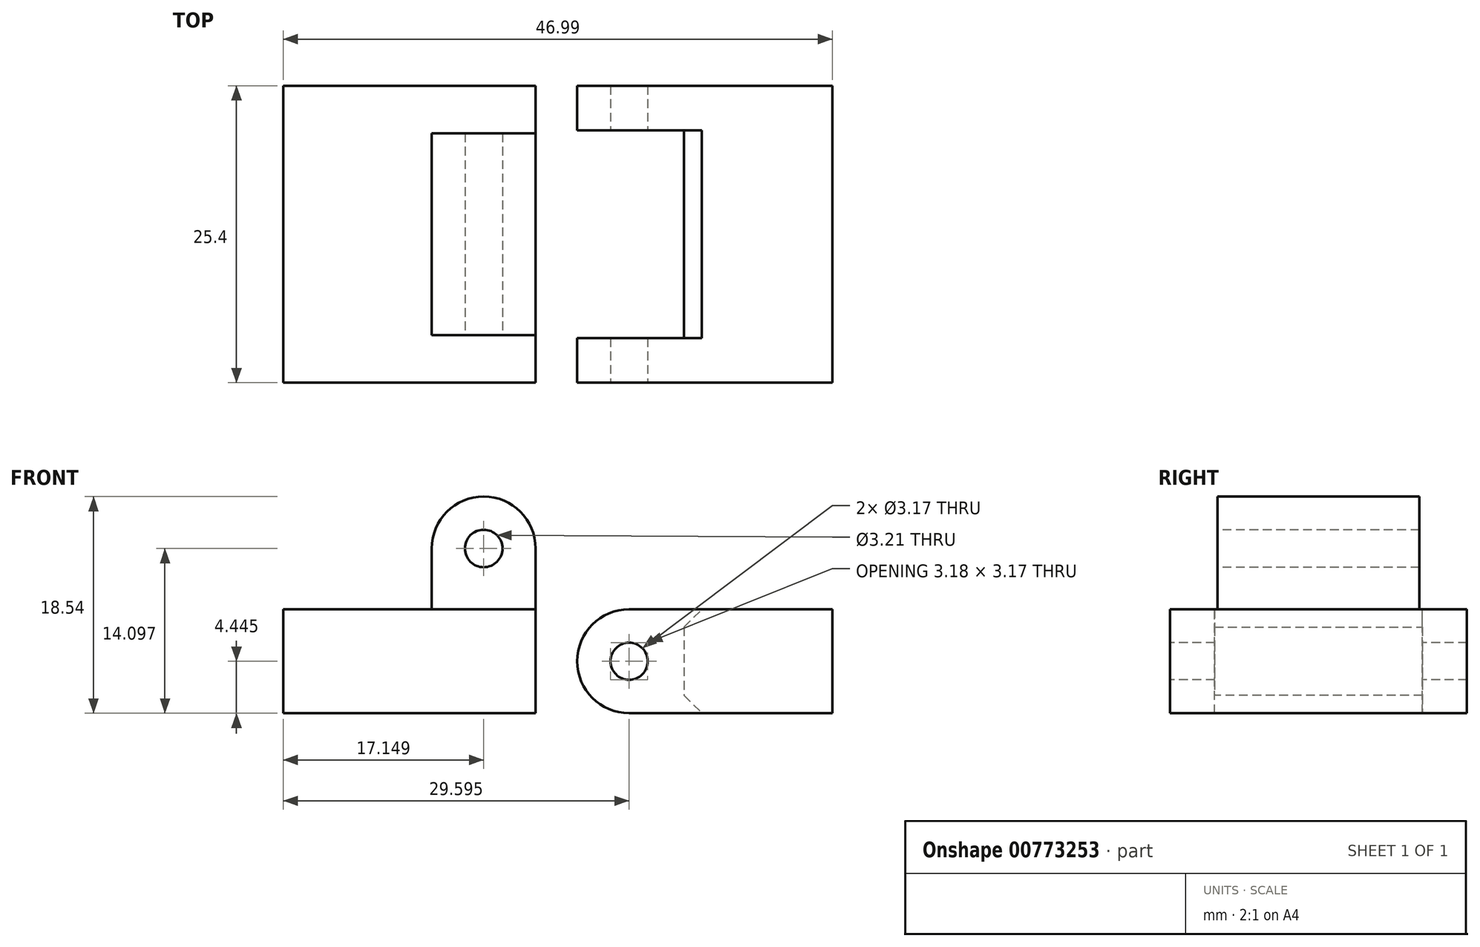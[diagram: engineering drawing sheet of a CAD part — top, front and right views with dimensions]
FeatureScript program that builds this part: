
annotation { "Feature Type Name" : "Feature", "Feature Type Description" : "" }
export const myFeature = defineFeature(function(context is Context, id is Id, definition is map)
    precondition{}
    {
        {
            var Q0;
            Q0=qCreatedBy(makeId("Top.planeOp"),FACE);
            var sketch = newSketch(context, id + "F0", { "sketchPlane" : qUnion([Q0])});
            skLineSegment(sketch, "E0.bottom", {"start": v(-16.8, 16.17) * mm, "end": v(-4.1, 16.17) * mm});
            skLineSegment(sketch, "E0.top", {"start": v(-16.8, -9.23) * mm, "end": v(-4.1, -9.23) * mm});
            skLineSegment(sketch, "E0.left", {"start": v(-16.8, 16.17) * mm, "end": v(-16.8, -9.23) * mm});
            skLineSegment(sketch, "E0.right", {"start": v(-4.1, 16.17) * mm, "end": v(-4.1, -9.23) * mm});
            skLineSegment(sketch, "E1", {"start": v(-16.8, 16.17) * mm, "end": v(-25.95, 16.17) * mm});
            skLineSegment(sketch, "E2", {"start": v(-16.8, -9.23) * mm, "end": v(-25.95, -9.23) * mm});
            skLineSegment(sketch, "E3", {"start": v(-25.95, -9.23) * mm, "end": v(-25.95, -5.42) * mm});
            skLineSegment(sketch, "E4", {"start": v(-25.95, -5.42) * mm, "end": v(-16.8, -5.42) * mm});
            skLineSegment(sketch, "E5", {"start": v(-25.95, 16.17) * mm, "end": v(-25.95, 12.36) * mm});
            skLineSegment(sketch, "E6", {"start": v(-25.95, 12.36) * mm, "end": v(-16.8, 12.36) * mm});
            skSolve(sketch);
        }
        {
            var Q0;
            {var subQ3=sQuery(id+"F0.wireOp",EDGE,"E0.bottom");Q0=makeQuery(id+"F0.imprint","IMPRINT",FACE,{"disambiguationData":[TD([[makeQuery(id+"F0.imprint","IMPRINT",EDGE,{"derivedFrom":subQ3}),-1.0]])]});}
            var Q1;
            {var subQ0=sQuery(id+"F0.wireOp",EDGE,"E1");Q1=makeQuery(id+"F0.imprint","IMPRINT",FACE,{"disambiguationData":[TD([[makeQuery(id+"F0.imprint","IMPRINT",EDGE,{"derivedFrom":subQ0}),1.0]])]});}
            var Q2;
            {var subQ0=sQuery(id+"F0.wireOp",EDGE,"E2");Q2=makeQuery(id+"F0.imprint","IMPRINT",FACE,{"disambiguationData":[TD([[makeQuery(id+"F0.imprint","IMPRINT",EDGE,{"derivedFrom":subQ0}),-1.0]])]});}
            extrude(context, id + "F1", {"entities" : qUnion([Q0, Q1, Q2]), "depth" : 8.9 * mm, "offsetDistance" : 25.4 * mm});
        }
        {
            var Q0;
            Q0=qCreatedBy(makeId("Top.planeOp"),FACE);
            var sketch = newSketch(context, id + "F2", { "sketchPlane" : qUnion([Q0])});
            skPoint(sketch, "E7.0", {"position": v(-25.95, 16.17) * mm});
            skPoint(sketch, "E7.1", {"position": v(-25.95, -9.23) * mm});
            skLineSegment(sketch, "E8", {"start": v(-38.4, 16.17) * mm, "end": v(-38.4, 12.1) * mm});
            skLineSegment(sketch, "E9", {"start": v(-38.4, 12.1) * mm, "end": v(-29.5, 12.1) * mm});
            skLineSegment(sketch, "E10", {"start": v(-38.4, 12.1) * mm, "end": v(-38.4, -9.23) * mm, "construction": true});
            skLineSegment(sketch, "E11", {"start": v(-38.4, -9.23) * mm, "end": v(-38.4, -5.17) * mm});
            skLineSegment(sketch, "E12", {"start": v(-38.4, -5.17) * mm, "end": v(-29.5, -5.17) * mm});
            skLineSegment(sketch, "E13", {"start": v(-29.5, -5.17) * mm, "end": v(-29.5, 12.1) * mm});
            skLineSegment(sketch, "E14", {"start": v(-38.4, 16.17) * mm, "end": v(-51.1, 16.17) * mm});
            skLineSegment(sketch, "E15", {"start": v(-51.1, 16.17) * mm, "end": v(-51.1, -9.23) * mm});
            skLineSegment(sketch, "E16", {"start": v(-51.1, -9.23) * mm, "end": v(-38.4, -9.23) * mm});
            skPoint(sketch, "E17.0", {"position": v(-16.8, 3.47) * mm});
            skLineSegment(sketch, "E18", {"start": v(-16.8, 3.47) * mm, "end": v(-29.5, 3.47) * mm, "construction": true});
            skSolve(sketch);
        }
        {
            var Q0;
            Q0=makeQuery(id+"F2.imprint","IMPRINT",FACE,{"disambiguationData":[TD([[makeQuery(id+"F2.imprint","IMPRINT",EDGE,{"derivedFrom":sQuery(id+"F2.wireOp",EDGE,"E8")}),-1.0]])]});
            extrude(context, id + "F3", {"entities" : qUnion([Q0]), "depth" : 8.9 * mm, "offsetDistance" : 25.4 * mm});
        }
        {
            var Q0;
            Q0=makeQuery(id+"F3.opExtrude","CAP_FACE",FACE,{"disambiguationData":[OSD([sQuery(id+"F2.wireOp",EDGE,"E8"),sQuery(id+"F2.wireOp",EDGE,"E9"),sQuery(id+"F2.wireOp",EDGE,"E11"),sQuery(id+"F2.wireOp",EDGE,"E12"),sQuery(id+"F2.wireOp",EDGE,"E13"),sQuery(id+"F2.wireOp",EDGE,"E14"),sQuery(id+"F2.wireOp",EDGE,"E15"),sQuery(id+"F2.wireOp",EDGE,"E16")])],"isStart":false});
            var sketch = newSketch(context, id + "F4", { "sketchPlane" : qUnion([Q0])});
            skLineSegment(sketch, "E19.0", {"start": v(-38.4, -5.17) * mm, "end": v(-29.5, -5.17) * mm});
            skLineSegment(sketch, "E19.1", {"start": v(-29.5, -5.17) * mm, "end": v(-29.5, 12.1) * mm});
            skLineSegment(sketch, "E19.2", {"start": v(-38.4, 12.1) * mm, "end": v(-29.5, 12.1) * mm});
            skLineSegment(sketch, "E20", {"start": v(-38.4, -5.17) * mm, "end": v(-38.4, 12.1) * mm});
            skSolve(sketch);
        }
        {
            var Q0;
            Q0=makeQuery(id+"F4.imprint","IMPRINT",FACE,{"disambiguationData":[TD([[makeQuery(id+"F4.imprint","IMPRINT",EDGE,{"derivedFrom":sQuery(id+"F4.wireOp",EDGE,"E19.0")}),1.0]])]});
            extrude(context, id + "F5", {"entities" : qUnion([Q0]), "operationType" : NewBodyOperationType.ADD, "depth" : 9.65 * mm, "offsetDistance" : 25.4 * mm});
        }
        {
            var Q0;
            Q0=makeQuery(id+"F5.boolean.opBoolean","MERGE",FACE,{"derivedFrom":[makeQuery(id+"F3.opExtrude","SWEPT_FACE",FACE,{"disambiguationData":[OSD([sQuery(id+"F2.wireOp",EDGE,"E12")])]}),makeQuery(id+"F5.opExtrude","SWEPT_FACE",FACE,{"disambiguationData":[OSD([sQuery(id+"F4.wireOp",EDGE,"E19.0")])]})]});
            var sketch = newSketch(context, id + "F6", { "sketchPlane" : qUnion([Q0])});
            skLineSegment(sketch, "E21", {"start": v(-33.95, 18.54) * mm, "end": v(-33.95, 14.1) * mm, "construction": true});
            skCircle(sketch, "E22", {"center": v(-33.95, 14.1) * mm, "radius": 1.6 * mm});
            skSolve(sketch);
        }
        {
            var Q0;
            Q0=makeQuery(id+"F6.imprint","IMPRINT",FACE,{"disambiguationData":[TD([[makeQuery(id+"F6.imprint","IMPRINT",EDGE,{"derivedFrom":sQuery(id+"F6.wireOp",EDGE,"E22")}),1.0]])]});
            extrude(context, id + "F7", {"entities" : qUnion([Q0]), "operationType" : NewBodyOperationType.REMOVE, "oppositeDirection" : true, "depth" : 25.4 * mm, "offsetDistance" : 25.4 * mm});
        }
        {
            var Q0;
            Q0=makeQuery(id+"F1.opExtrude","SWEPT_FACE",FACE,{"disambiguationData":[OSD([sQuery(id+"F0.wireOp",EDGE,"E0.top"),sQuery(id+"F0.wireOp",EDGE,"E2")])]});
            var sketch = newSketch(context, id + "F8", { "sketchPlane" : qUnion([Q0])});
            skLineSegment(sketch, "E23", {"start": v(-25.95, 4.45) * mm, "end": v(-21.5, 4.45) * mm, "construction": true});
            skCircle(sketch, "E24", {"center": v(-21.5, 4.45) * mm, "radius": 1.59 * mm});
            skSolve(sketch);
        }
        {
            var Q0;
            Q0=makeQuery(id+"F8.imprint","IMPRINT",FACE,{"disambiguationData":[TD([[makeQuery(id+"F8.imprint","IMPRINT",EDGE,{"derivedFrom":sQuery(id+"F8.wireOp",EDGE,"E24")}),1.0]])]});
            extrude(context, id + "F9", {"entities" : qUnion([Q0]), "operationType" : NewBodyOperationType.REMOVE, "oppositeDirection" : true, "depth" : 25.4 * mm, "offsetDistance" : 25.4 * mm});
        }
        {
            var Q0;
            Q0=makeQuery(id+"F5.opExtrude","CAP_EDGE",EDGE,{"disambiguationData":[OSD([sQuery(id+"F4.wireOp",EDGE,"E19.1")])],"isStart":false});
            var Q1;
            Q1=makeQuery(id+"F5.opExtrude","CAP_EDGE",EDGE,{"disambiguationData":[OSD([sQuery(id+"F4.wireOp",EDGE,"E20")])],"isStart":false});
            var Q2;
            Q2=makeQuery(id+"F1.opExtrude","CAP_EDGE",EDGE,{"disambiguationData":[OSD([sQuery(id+"F0.wireOp",EDGE,"E3")])],"isStart":false});
            var Q3;
            Q3=makeQuery(id+"F1.opExtrude","CAP_EDGE",EDGE,{"disambiguationData":[OSD([sQuery(id+"F0.wireOp",EDGE,"E3")])],"isStart":true});
            var Q4;
            Q4=makeQuery(id+"F1.opExtrude","CAP_EDGE",EDGE,{"disambiguationData":[OSD([sQuery(id+"F0.wireOp",EDGE,"E5")])],"isStart":true});
            var Q5;
            Q5=makeQuery(id+"F1.opExtrude","CAP_EDGE",EDGE,{"disambiguationData":[OSD([sQuery(id+"F0.wireOp",EDGE,"E5")])],"isStart":false});
            fillet(context, id + "F10", {"entities" : qUnion([Q0, Q1, Q2, Q3, Q4, Q5]), "radius" : 4.44 * mm, "tangentPropagation" : true, "allowEdgeOverflow" : false});
        }
        {
            var Q0;
            Q0=makeQuery(id+"F1.opExtrude","CAP_EDGE",EDGE,{"disambiguationData":[OSD([sQuery(id+"F0.wireOp",EDGE,"E0.left")])],"isStart":false});
            var Q1;
            Q1=makeQuery(id+"F1.opExtrude","CAP_EDGE",EDGE,{"disambiguationData":[OSD([sQuery(id+"F0.wireOp",EDGE,"E0.left")])],"isStart":true});
            chamfer(context, id + "F11", {"entities" : qUnion([Q0, Q1]), "width" : 1.52 * mm, "tangentPropagation" : true});
        }
        {
            var Q0;
            Q0=makeQuery(id+"F3.opExtrude","SWEPT_FACE",FACE,{"disambiguationData":[OSD([sQuery(id+"F2.wireOp",EDGE,"E11")])]});
            var Q1;
            Q1=makeQuery(id+"F3.opExtrude","SWEPT_FACE",FACE,{"disambiguationData":[OSD([sQuery(id+"F2.wireOp",EDGE,"E8")])]});
            var Q2;
            Q2=makeQuery(id+"F5.boolean.opBoolean","MERGE",FACE,{"derivedFrom":[makeQuery(id+"F3.opExtrude","SWEPT_FACE",FACE,{"disambiguationData":[OSD([sQuery(id+"F2.wireOp",EDGE,"E13")])]}),makeQuery(id+"F5.opExtrude","SWEPT_FACE",FACE,{"disambiguationData":[OSD([sQuery(id+"F4.wireOp",EDGE,"E19.1")])]})]});
            extrude(context, id + "F12", {"entities" : qUnion([Q0, Q1]), "operationType" : NewBodyOperationType.ADD, "endBound" : BoundingType.UP_TO_SURFACE, "depth" : 25.4 * mm, "endBoundEntityFace" : qUnion([Q2]), "offsetDistance" : 25.4 * mm});
        }
    });
